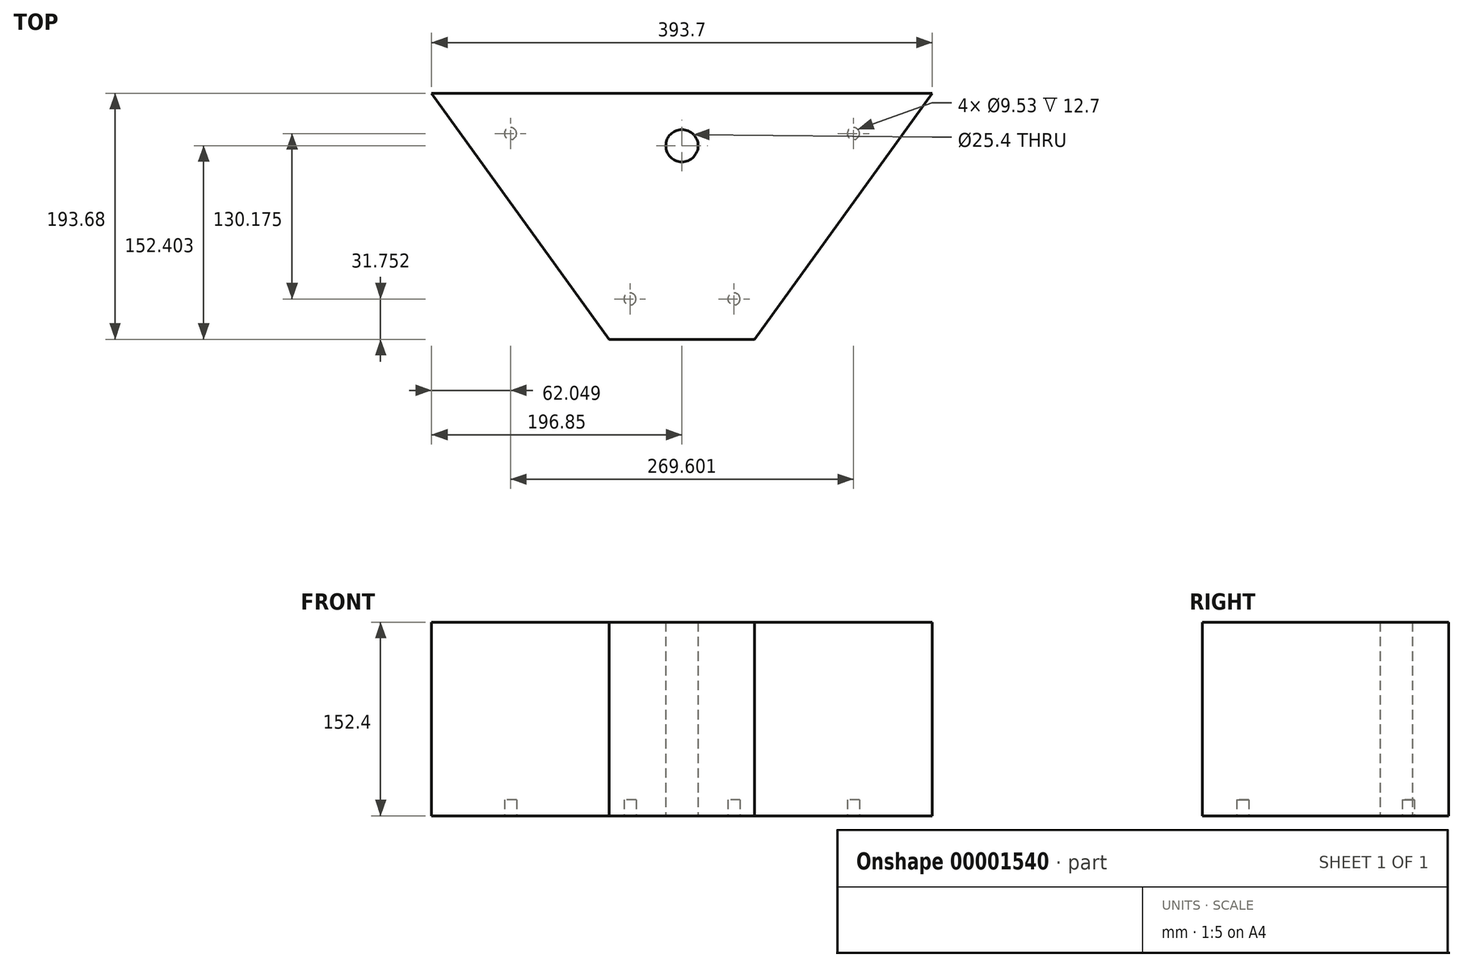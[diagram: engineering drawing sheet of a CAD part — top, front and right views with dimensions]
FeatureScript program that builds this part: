
annotation { "Feature Type Name" : "Feature", "Feature Type Description" : "" }
export const myFeature = defineFeature(function(context is Context, id is Id, definition is map)
    precondition{}
    {
        {
            var Q0;
            Q0=qCreatedBy(makeId("Top.planeOp"),FACE);
            var sketch = newSketch(context, id + "F0", { "sketchPlane" : qUnion([Q0])});
            skLineSegment(sketch, "E0", {"start": v(-196.85, 96.84) * mm, "end": v(196.85, 96.84) * mm});
            skLineSegment(sketch, "E1", {"start": v(-57.15, -96.84) * mm, "end": v(57.15, -96.84) * mm});
            skLineSegment(sketch, "E2", {"start": v(-196.85, 96.84) * mm, "end": v(-57.15, -96.84) * mm});
            skLineSegment(sketch, "E3", {"start": v(196.85, 96.84) * mm, "end": v(57.15, -96.84) * mm});
            skCircle(sketch, "E4", {"center": v(0, 55.56) * mm, "radius": 12.7 * mm});
            skLineSegment(sketch, "E5.0", {"start": v(-134.8, 65.09) * mm, "end": v(134.8, 65.09) * mm, "construction": true});
            skLineSegment(sketch, "E5.1", {"start": v(-134.8, 65.09) * mm, "end": v(-40.9, -65.09) * mm, "construction": true});
            skLineSegment(sketch, "E5.2", {"start": v(-40.9, -65.09) * mm, "end": v(40.9, -65.09) * mm, "construction": true});
            skLineSegment(sketch, "E5.3", {"start": v(134.8, 65.09) * mm, "end": v(40.9, -65.09) * mm, "construction": true});
            skCircle(sketch, "E6", {"center": v(-134.8, 65.09) * mm, "radius": 4.76 * mm});
            skCircle(sketch, "E7", {"center": v(-40.9, -65.09) * mm, "radius": 4.76 * mm});
            skCircle(sketch, "E8", {"center": v(40.9, -65.09) * mm, "radius": 4.76 * mm});
            skCircle(sketch, "E9", {"center": v(134.8, 65.09) * mm, "radius": 4.76 * mm});
            skSolve(sketch);
        }
        {
            var Q0;
            Q0=makeQuery(id+"F0.imprint","IMPRINT",FACE,{"disambiguationData":[TD([[makeQuery(id+"F0.imprint","IMPRINT",EDGE,{"derivedFrom":sQuery(id+"F0.wireOp",EDGE,"E0")}),-1.0]])]});
            var Q1;
            Q1=makeQuery(id+"F0.imprint","IMPRINT",FACE,{"disambiguationData":[TD([[makeQuery(id+"F0.imprint","IMPRINT",EDGE,{"derivedFrom":sQuery(id+"F0.wireOp",EDGE,"E9")}),1.0]])]});
            var Q2;
            Q2=makeQuery(id+"F0.imprint","IMPRINT",FACE,{"disambiguationData":[TD([[makeQuery(id+"F0.imprint","IMPRINT",EDGE,{"derivedFrom":sQuery(id+"F0.wireOp",EDGE,"E6")}),1.0]])]});
            var Q3;
            Q3=makeQuery(id+"F0.imprint","IMPRINT",FACE,{"disambiguationData":[TD([[makeQuery(id+"F0.imprint","IMPRINT",EDGE,{"derivedFrom":sQuery(id+"F0.wireOp",EDGE,"E7")}),1.0]])]});
            var Q4;
            Q4=makeQuery(id+"F0.imprint","IMPRINT",FACE,{"disambiguationData":[TD([[makeQuery(id+"F0.imprint","IMPRINT",EDGE,{"derivedFrom":sQuery(id+"F0.wireOp",EDGE,"E8")}),1.0]])]});
            extrude(context, id + "F1", {"entities" : qUnion([Q0, Q1, Q2, Q3, Q4]), "depth" : 152.4 * mm});
        }
        {
            var Q0;
            Q0=makeQuery(id+"F0.imprint","IMPRINT",FACE,{"disambiguationData":[TD([[makeQuery(id+"F0.imprint","IMPRINT",EDGE,{"derivedFrom":sQuery(id+"F0.wireOp",EDGE,"E6")}),1.0]])]});
            var Q1;
            Q1=makeQuery(id+"F0.imprint","IMPRINT",FACE,{"disambiguationData":[TD([[makeQuery(id+"F0.imprint","IMPRINT",EDGE,{"derivedFrom":sQuery(id+"F0.wireOp",EDGE,"E9")}),1.0]])]});
            var Q2;
            Q2=makeQuery(id+"F0.imprint","IMPRINT",FACE,{"disambiguationData":[TD([[makeQuery(id+"F0.imprint","IMPRINT",EDGE,{"derivedFrom":sQuery(id+"F0.wireOp",EDGE,"E8")}),1.0]])]});
            var Q3;
            Q3=makeQuery(id+"F0.imprint","IMPRINT",FACE,{"disambiguationData":[TD([[makeQuery(id+"F0.imprint","IMPRINT",EDGE,{"derivedFrom":sQuery(id+"F0.wireOp",EDGE,"E7")}),1.0]])]});
            extrude(context, id + "F2", {"entities" : qUnion([Q0, Q1, Q2, Q3]), "operationType" : NewBodyOperationType.REMOVE, "depth" : 12.7 * mm});
        }
    });
